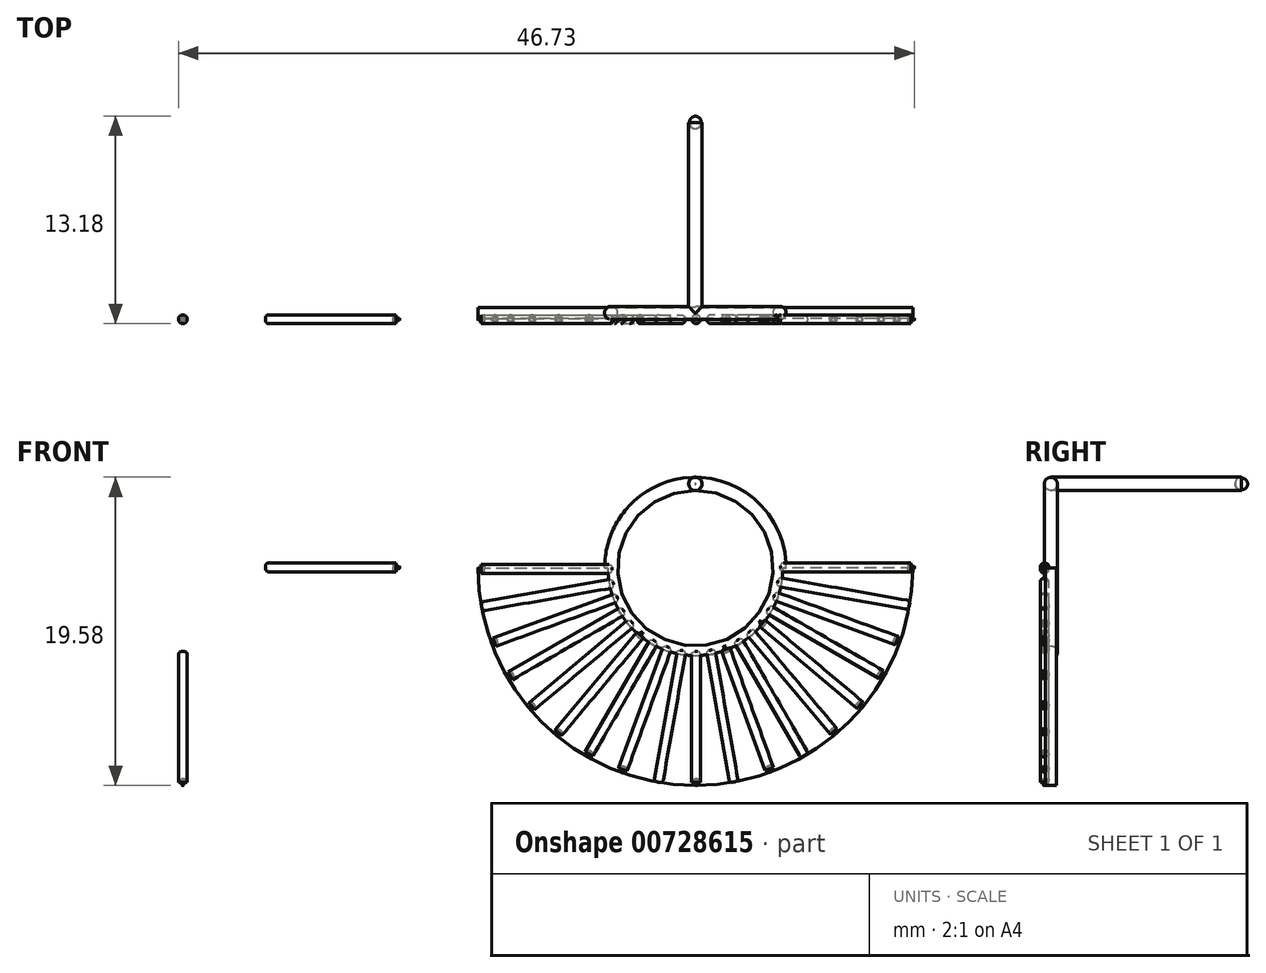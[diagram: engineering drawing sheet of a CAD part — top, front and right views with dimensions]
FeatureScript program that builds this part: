
annotation { "Feature Type Name" : "Feature", "Feature Type Description" : "" }
export const myFeature = defineFeature(function(context is Context, id is Id, definition is map)
    precondition{}
    {
        {
            var Q0;
            Q0=qCreatedBy(makeId("Front.planeOp"),FACE);
            var sketch = newSketch(context, id + "F0", { "sketchPlane" : qUnion([Q0])});
            skCircle(sketch, "E0", {"center": v(0, 0) * mm, "radius": 5.45 * mm});
            skSolve(sketch);
        }
        {
            var Q0;
            Q0=qCreatedBy(makeId("Top.planeOp"),FACE);
            var sketch = newSketch(context, id + "F1", { "sketchPlane" : qUnion([Q0])});
            skCircle(sketch, "E1", {"center": v(5.35, 0) * mm, "radius": 0.41 * mm});
            skSolve(sketch);
        }
        {
            var Q0;
            Q0 = qSketchRegion(id + "F1", true);
            var Q1;
            Q1=sQuery(id+"F0.wireOp",EDGE,"E0");
            revolve(context, id + "F2", {"surfaceOperationType" : NewSurfaceOperationType.NEW, "entities" : qUnion([Q0]), "axis" : qUnion([Q1]), "revolveType" : RevolveType.FULL});
        }
        {
            var Q0;
            Q0=qCreatedBy(makeId("Top.planeOp"),FACE);
            var sketch = newSketch(context, id + "F3", { "sketchPlane" : qUnion([Q0])});
            skLineSegment(sketch, "E2.bottom", {"start": v(-13.8, 0.34) * mm, "end": v(-5.52, 0.34) * mm});
            skLineSegment(sketch, "E2.top", {"start": v(-13.8, -0.36) * mm, "end": v(-5.52, -0.36) * mm});
            skLineSegment(sketch, "E2.left", {"start": v(-13.8, 0.34) * mm, "end": v(-13.8, -0.36) * mm});
            skLineSegment(sketch, "E2.right", {"start": v(-5.52, 0.34) * mm, "end": v(-5.52, -0.36) * mm});
            skSolve(sketch);
        }
        {
            var Q0;
            Q0 = qSketchRegion(id + "F3", true);
            var Q1;
            Q1=makeQuery(id+"F2.opRevolve","SWEPT_FACE",FACE,{"disambiguationData":[OSD([sQuery(id+"F1.wireOp",EDGE,"E1")])]});
            revolve(context, id + "F4", {"operationType" : NewBodyOperationType.ADD, "surfaceOperationType" : NewSurfaceOperationType.NEW, "entities" : qUnion([Q0]), "axis" : qUnion([Q1]), "revolveType" : RevolveType.ONE_DIRECTION, "oppositeDirection" : true, "angle" : 180 * degree});
        }
        {
            var Q0;
            Q0=qCreatedBy(makeId("Top.planeOp"),FACE);
            var sketch = newSketch(context, id + "F5", { "sketchPlane" : qUnion([Q0])});
            skCircle(sketch, "E3", {"center": v(23.55, 0) * mm, "radius": 0.28 * mm});
            skSolve(sketch);
        }
        {
            var Q0;
            Q0=makeQuery(id+"F5.imprint","IMPRINT",FACE,{"disambiguationData":[TD([[makeQuery(id+"F5.imprint","IMPRINT",EDGE,{"derivedFrom":sQuery(id+"F5.wireOp",EDGE,"E3")}),1.0]])]});
            extrude(context, id + "F6", {"entities" : qUnion([Q0]), "oppositeDirection" : true, "depth" : 8.5 * mm, "offsetDistance" : 25 * mm});
        }
        {
            var Q0;
            Q0=makeQuery(id+"F6.opExtrude","CAP_EDGE",EDGE,{"disambiguationData":[OSD([sQuery(id+"F5.wireOp",EDGE,"E3")])],"isStart":false});
            var Q1;
            Q1=makeQuery(id+"F6.opExtrude","CAP_EDGE",EDGE,{"disambiguationData":[OSD([sQuery(id+"F5.wireOp",EDGE,"E3")])],"isStart":true});
            fillet(context, id + "F7", {"entities" : qUnion([Q0, Q1]), "radius" : .2 * mm, "tangentPropagation" : true, "allowEdgeOverflow" : false});
        }
        {
            var Q0;
            Q0=makeQuery(id+"F6.opExtrude","SWEPT_BODY",BODY,{"disambiguationData":[OSD([sQuery(id+"F5.wireOp",EDGE,"E3")])]});
            transform(context, id + "F8", {"entities" : qUnion([Q0]), "transformType" : TransformType.TRANSLATION_3D, "dx" : -23.5 * mm, "dy" : -0.4 * mm, "dz" : -5.3 * mm, "makeCopy" : false});
        }
        {
            var Q0;
            Q0=makeQuery(id+"F6.opExtrude","SWEPT_BODY",BODY,{"disambiguationData":[OSD([sQuery(id+"F5.wireOp",EDGE,"E3")])]});
            var Q1;
            Q1=makeQuery(id+"F2.opRevolve","SWEPT_FACE",FACE,{"disambiguationData":[OSD([sQuery(id+"F1.wireOp",EDGE,"E1")])]});
            circularPattern(context, id + "F9", {"entities" : qUnion([Q0]), "axis" : qUnion([Q1]), "angle" : 90 * degree, "instanceCount" : 10, "equalSpace" : true});
        }
        {
            var Q0;
            Q0=makeQuery(id+"F6.opExtrude","SWEPT_BODY",BODY,{"disambiguationData":[OSD([sQuery(id+"F5.wireOp",EDGE,"E3")])]});
            var Q1;
            Q1=makeQuery(id+"F2.opRevolve","SWEPT_FACE",FACE,{"disambiguationData":[OSD([sQuery(id+"F1.wireOp",EDGE,"E1")])]});
            circularPattern(context, id + "F10", {"entities" : qUnion([Q0]), "axis" : qUnion([Q1]), "angle" : 90 * degree, "instanceCount" : 10, "oppositeDirection" : true, "equalSpace" : true});
        }
        {
            var Q0;
            Q0=qCreatedBy(makeId("Front.planeOp"),FACE);
            var sketch = newSketch(context, id + "F11", { "sketchPlane" : qUnion([Q0])});
            skCircle(sketch, "E4", {"center": v(0, 5.35) * mm, "radius": 0.43 * mm});
            skSolve(sketch);
        }
        {
            var Q0;
            Q0 = qSketchRegion(id + "F11", true);
            extrude(context, id + "F12", {"entities" : qUnion([Q0]), "operationType" : NewBodyOperationType.ADD, "oppositeDirection" : true, "depth" : 12.5 * mm, "offsetDistance" : 25 * mm});
        }
        {
            var Q0;
            Q0=makeQuery(id+"F12.opExtrude","CAP_FACE",FACE,{"disambiguationData":[OSD([sQuery(id+"F11.wireOp",EDGE,"E4")])],"isStart":false});
            fillet(context, id + "F13", {"entities" : qUnion([Q0]), "radius" : .4 * mm, "tangentPropagation" : true, "allowEdgeOverflow" : false});
        }
        {
            var Q0;
            Q0=makeQuery(id+"F6.opExtrude","SWEPT_BODY",BODY,{"disambiguationData":[OSD([sQuery(id+"F5.wireOp",EDGE,"E3")])]});
            transform(context, id + "F14", {"entities" : qUnion([Q0]), "transformType" : TransformType.COPY});
        }
        {
            var Q0;
            Q0=makeQuery(id+"F6.opExtrude","SWEPT_BODY",BODY,{"disambiguationData":[OSD([sQuery(id+"F5.wireOp",EDGE,"E3")])]});
            transform(context, id + "F15", {"entities" : qUnion([Q0]), "transformType" : TransformType.TRANSLATION_3D, "dx" : -32.6 * mm, "dy" : 0 * mm, "dz" : 0 * mm, "makeCopy" : false});
        }
        {
            var Q0;
            Q0=makeQuery(id+"F10.opPattern","COPY",BODY,{"derivedFrom":makeQuery(id+"F6.opExtrude","SWEPT_BODY",BODY,{"disambiguationData":[OSD([sQuery(id+"F5.wireOp",EDGE,"E3")])]}),"instanceName":"9"});
            transform(context, id + "F16", {"entities" : qUnion([Q0]), "transformType" : TransformType.TRANSLATION_3D, "dx" : -32.6 * mm, "dy" : 0 * mm, "dz" : 0 * mm, "makeCopy" : false});
        }
        {
            var Q0;
            Q0=makeQuery(id+"F10.opPattern","COPY",BODY,{"derivedFrom":makeQuery(id+"F6.opExtrude","SWEPT_BODY",BODY,{"disambiguationData":[OSD([sQuery(id+"F5.wireOp",EDGE,"E3")])]}),"instanceName":"9"});
            transform(context, id + "F17", {"entities" : qUnion([Q0]), "transformType" : TransformType.COPY});
        }
        {
            var Q0;
            Q0=makeQuery(id+"F10.opPattern","COPY",BODY,{"derivedFrom":makeQuery(id+"F6.opExtrude","SWEPT_BODY",BODY,{"disambiguationData":[OSD([sQuery(id+"F5.wireOp",EDGE,"E3")])]}),"instanceName":"9"});
            transform(context, id + "F18", {"entities" : qUnion([Q0]), "transformType" : TransformType.TRANSLATION_3D, "dx" : 32.7 * mm, "dy" : 0 * mm, "dz" : 0 * mm, "makeCopy" : false});
        }
    });
